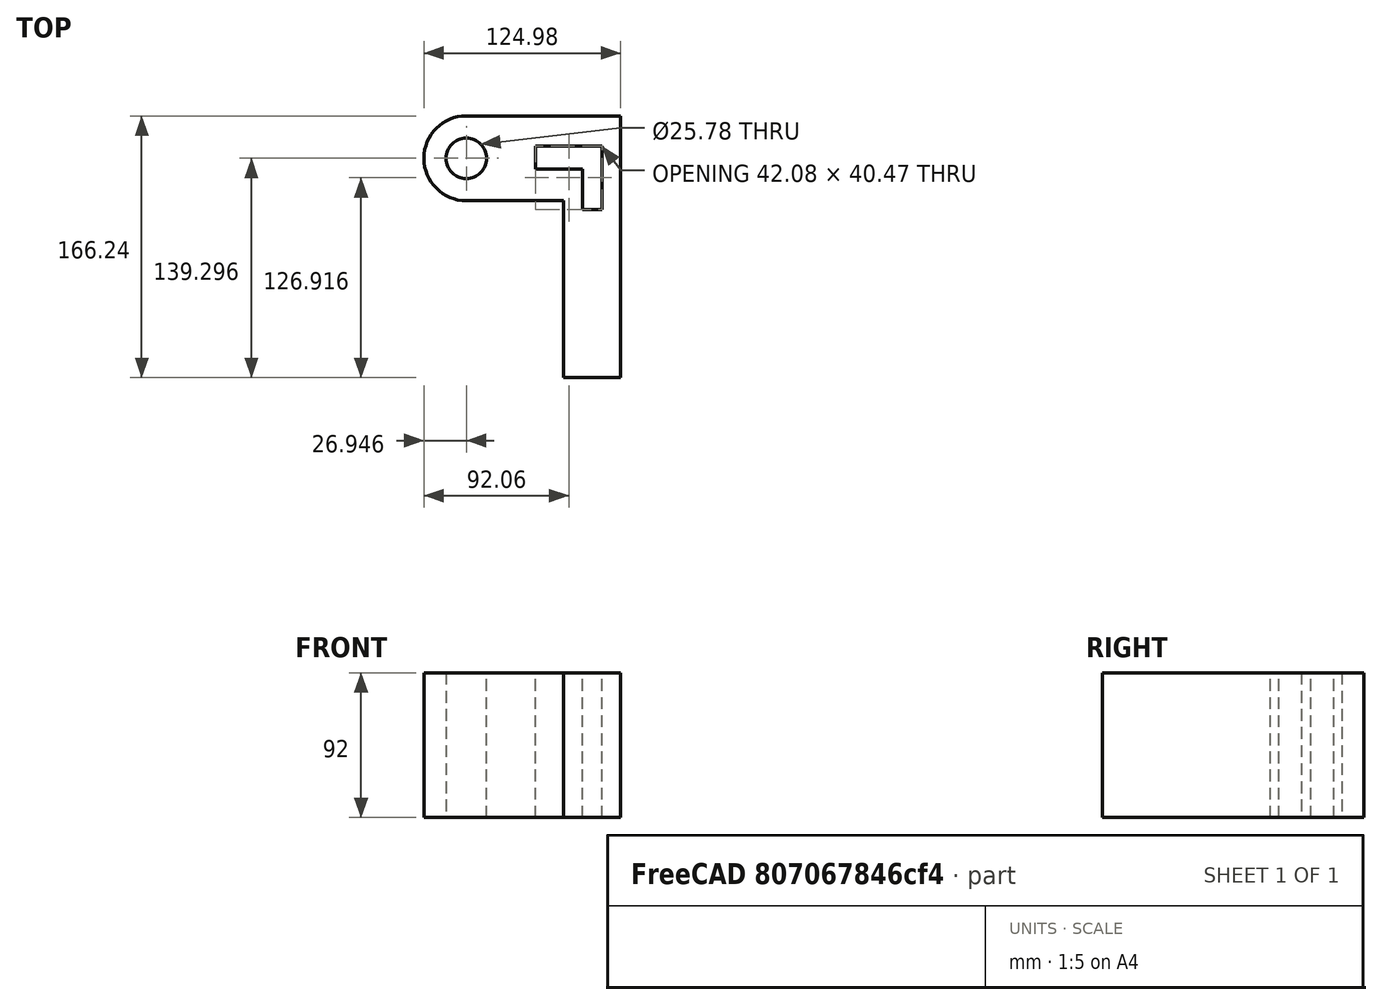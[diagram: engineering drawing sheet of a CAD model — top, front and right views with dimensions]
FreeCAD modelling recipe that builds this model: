
FCSTD DOCUMENT
Label: Fem2
License: CC-BY 3.0
LicenseURL: http://creativecommons.org/licenses/by/3.0/
objects: Sketcher::SketchObject×1, PartDesign::Pad×1, Fem::FemMeshShapeNetgenObject×1, Fem::FemAnalysis×1
note: 3 computed .brp shape members not serialized (recipe doc carries the construction recipe); baked Part::Feature solids carry a one-line shape summary decoded from their .brp

FEATURE [Sketcher::SketchObject] Sketch
  sketch-geometry (13):
    g0: ArcOfCircle CenterX=-29.9237 CenterY=19.9863 CenterZ=0 NormalX=0 NormalY=0 NormalZ=1 Radius=26.9466 StartAngle=1.5708 EndAngle=4.71239
    g1: LineSegment StartX=-29.9237 StartY=46.933 StartZ=0 EndX=68.1073 EndY=46.933 EndZ=0
    g2: LineSegment StartX=68.1073 StartY=46.933 StartZ=0 EndX=68.1073 EndY=-119.309 EndZ=0
    g3: LineSegment StartX=68.1073 StartY=-119.309 StartZ=0 EndX=31.7141 EndY=-119.309 EndZ=0
    g4: LineSegment StartX=31.7141 StartY=-119.309 StartZ=0 EndX=31.7141 EndY=-6.96029 EndZ=0
    g5: LineSegment StartX=31.7141 StartY=-6.96029 StartZ=0 EndX=-29.9236 EndY=-6.96029 EndZ=0
    g6: Circle CenterX=-29.9237 CenterY=19.9863 CenterZ=0 NormalX=0 NormalY=0 NormalZ=1 Radius=12.8881
    g7: LineSegment StartX=14.1478 StartY=27.839 StartZ=0 EndX=56.2317 EndY=27.839 EndZ=0
    g8: LineSegment StartX=56.2317 StartY=27.839 StartZ=0 EndX=56.2317 EndY=-12.6263 EndZ=0
    g9: LineSegment StartX=56.2317 StartY=-12.6263 StartZ=0 EndX=43.9303 EndY=-12.6263 EndZ=0
    g10: LineSegment StartX=43.9303 StartY=-12.6263 StartZ=0 EndX=43.9303 EndY=13.2715 EndZ=0
    g11: LineSegment StartX=43.9303 StartY=13.2715 StartZ=0 EndX=14.1478 EndY=13.2715 EndZ=0
    g12: LineSegment StartX=14.1478 StartY=13.2715 StartZ=0 EndX=14.1478 EndY=27.839 EndZ=0
  constraints (25):
    c: Tangent(g0,g1)
    c: Coincident(g1,g2)
    c: Vertical(g2)
    c: Coincident(g2,g3)
    c: Horizontal(g3)
    c: Coincident(g3,g4)
    c: Vertical(g4)
    c: Coincident(g4,g5)
    c: Coincident(g5,g0)
    c: Horizontal(g5)
    c: Horizontal(g1)
    c: Tangent(g0,g5)
    c: Coincident(g6,g0)
    c: Horizontal(g7)
    c: Coincident(g7,g8)
    c: Vertical(g8)
    c: Coincident(g8,g9)
    c: Horizontal(g9)
    c: Coincident(g9,g10)
    c: Vertical(g10)
    c: Coincident(g10,g11)
    c: Horizontal(g11)
    c: Coincident(g11,g12)
    c: Coincident(g12,g7)
    c: Vertical(g12)
FEATURE [PartDesign::Pad] Pad
  Length = 92
  Length2 = 100
  Sketch = -> Sketch
  Type = 0
FEATURE [Fem::FemMeshShapeNetgenObject] Pad_Mesh
  Fininess = 2
  GrothRate = 0.3
  MaxSize = 1000
  NbSegsPerEdge = 1
  NbSegsPerRadius = 2
  Optimize = true
  SecondOrder = false
  Shape = -> Pad
FEATURE [Fem::FemAnalysis] FemAnalysis
  Member = -> [Pad_Mesh]
